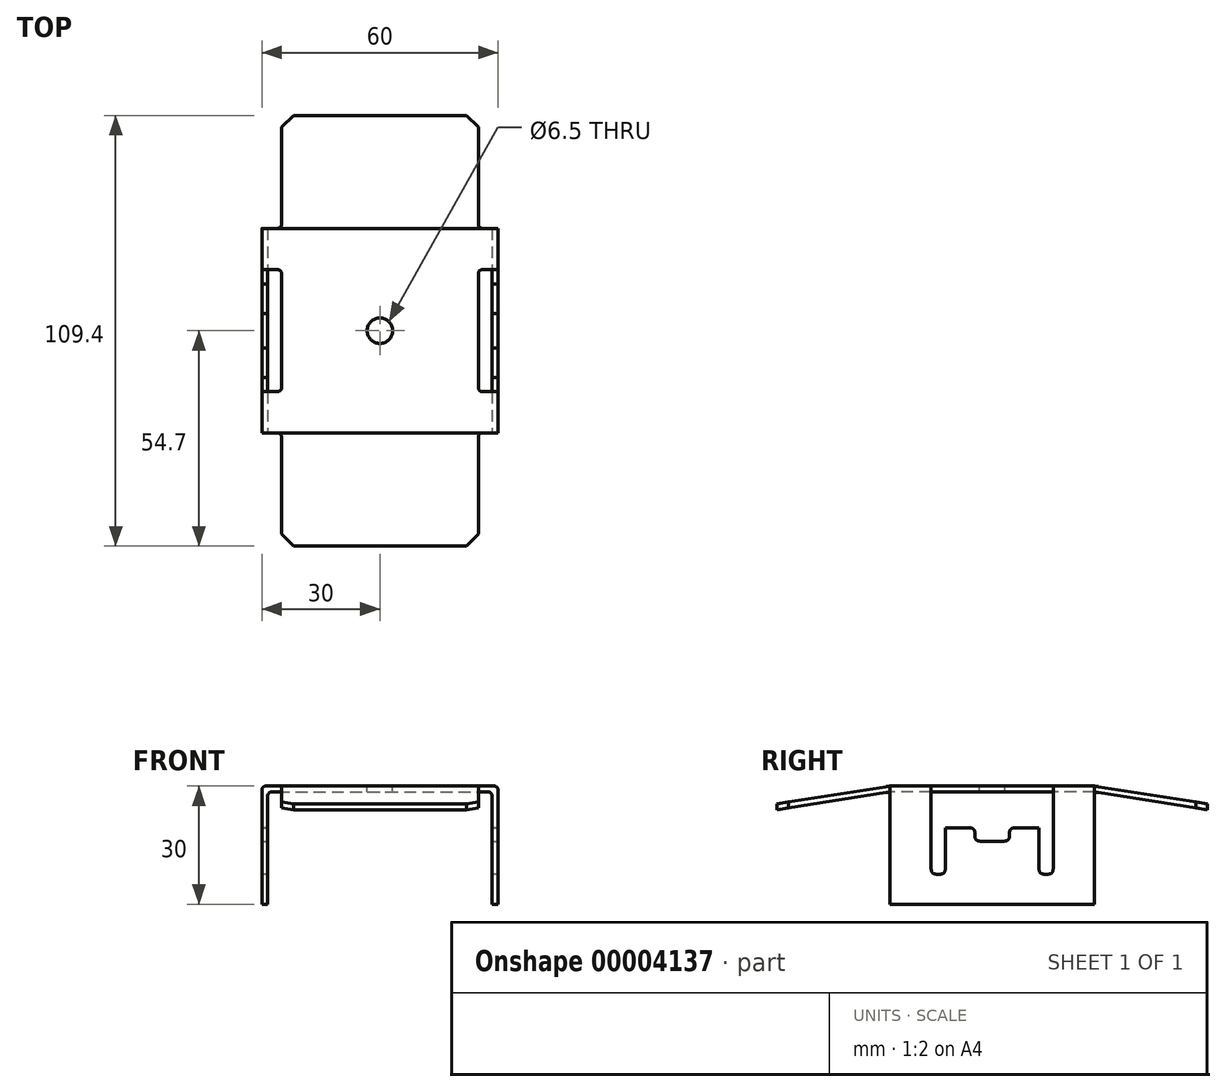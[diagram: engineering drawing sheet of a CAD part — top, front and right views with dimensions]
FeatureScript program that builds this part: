
annotation { "Feature Type Name" : "Feature", "Feature Type Description" : "" }
export const myFeature = defineFeature(function(context is Context, id is Id, definition is map)
    precondition{}
    {
        {
            var Q0;
            Q0=qCreatedBy(makeId("Top.planeOp"),FACE);
            var sketch = newSketch(context, id + "F0", { "sketchPlane" : qUnion([Q0])});
            skPoint(sketch, "E0.rect.middle", {"position": v(0, 0) * mm});
            skLineSegment(sketch, "E1", {"start": v(0, 54.7) * mm, "end": v(30, 54.7) * mm, "construction": true});
            skLineSegment(sketch, "E2", {"start": v(30, 54.7) * mm, "end": v(30, 0) * mm, "construction": true});
            skLineSegment(sketch, "E3", {"start": v(30, 0) * mm, "end": v(30, -54.7) * mm, "construction": true});
            skLineSegment(sketch, "E4", {"start": v(30, -54.7) * mm, "end": v(0, -54.7) * mm, "construction": true});
            skLineSegment(sketch, "E5", {"start": v(25, 54.7) * mm, "end": v(25, -54.7) * mm, "construction": true});
            skLineSegment(sketch, "E6", {"start": v(0, 15.5) * mm, "end": v(30, 15.5) * mm, "construction": true});
            skLineSegment(sketch, "E7", {"start": v(0, -15.5) * mm, "end": v(30, -15.5) * mm, "construction": true});
            skLineSegment(sketch, "E8", {"start": v(0, 26) * mm, "end": v(30, 26) * mm, "construction": true});
            skLineSegment(sketch, "E9", {"start": v(0, -26) * mm, "end": v(30, -26) * mm, "construction": true});
            skCircle(sketch, "E10", {"center": v(0, 0) * mm, "radius": 3.25 * mm});
            skLineSegment(sketch, "E11", {"start": v(0, 54.7) * mm, "end": v(25, 54.7) * mm});
            skLineSegment(sketch, "E12", {"start": v(25, 26) * mm, "end": v(30, 26) * mm});
            skLineSegment(sketch, "E13", {"start": v(30, -26) * mm, "end": v(25, -26) * mm});
            skLineSegment(sketch, "E14", {"start": v(25, -26) * mm, "end": v(25, -54.7) * mm});
            skLineSegment(sketch, "E15", {"start": v(0, -54.7) * mm, "end": v(25, -54.7) * mm});
            skLineSegment(sketch, "E16", {"start": v(30, -26) * mm, "end": v(30, -15.5) * mm});
            skLineSegment(sketch, "E17", {"start": v(30, 15.5) * mm, "end": v(30, 26) * mm});
            skLineSegment(sketch, "E18", {"start": v(25, 26) * mm, "end": v(25, 54.7) * mm});
            skLineSegment(sketch, "E19", {"start": v(30, 15.5) * mm, "end": v(30, -15.5) * mm});
            skLineSegment(sketch, "E20.0.MirrorCS", {"start": v(0, 54.7) * mm, "end": v(-25, 54.7) * mm});
            skLineSegment(sketch, "E20.1.MirrorCS", {"start": v(-25, 26) * mm, "end": v(-25, 54.7) * mm});
            skLineSegment(sketch, "E20.2.MirrorCS", {"start": v(-25, 26) * mm, "end": v(-30, 26) * mm});
            skLineSegment(sketch, "E20.3.MirrorCS", {"start": v(-30, 15.5) * mm, "end": v(-30, 26) * mm});
            skLineSegment(sketch, "E20.4.MirrorCS", {"start": v(-30, 15.5) * mm, "end": v(-30, -15.5) * mm});
            skLineSegment(sketch, "E20.5.MirrorCS", {"start": v(-30, -26) * mm, "end": v(-30, -15.5) * mm});
            skLineSegment(sketch, "E20.6.MirrorCS", {"start": v(-30, -26) * mm, "end": v(-25, -26) * mm});
            skLineSegment(sketch, "E20.7.MirrorCS", {"start": v(0, -54.7) * mm, "end": v(-25, -54.7) * mm});
            skLineSegment(sketch, "E20.8.MirrorCS", {"start": v(-25, -26) * mm, "end": v(-25, -54.7) * mm});
            skLineSegment(sketch, "E21", {"start": v(-30, -15.5) * mm, "end": v(-25, -15.5) * mm});
            skLineSegment(sketch, "E22", {"start": v(-25, -15.5) * mm, "end": v(-25, 15.5) * mm});
            skLineSegment(sketch, "E23", {"start": v(-25, 15.5) * mm, "end": v(-30, 15.5) * mm});
            skLineSegment(sketch, "E24", {"start": v(30, -15.5) * mm, "end": v(25, -15.5) * mm});
            skLineSegment(sketch, "E25", {"start": v(25, -15.5) * mm, "end": v(25, 15.5) * mm});
            skLineSegment(sketch, "E26", {"start": v(25, 15.5) * mm, "end": v(30, 15.5) * mm});
            skSolve(sketch);
        }
        {
            var Q0;
            Q0=qCreatedBy(makeId("Right.planeOp"),FACE);
            var sketch = newSketch(context, id + "F1", { "sketchPlane" : qUnion([Q0])});
            skLineSegment(sketch, "E27", {"start": v(0, -30) * mm, "end": v(26, -30) * mm});
            skLineSegment(sketch, "E28", {"start": v(15.5, -22.4) * mm, "end": v(11.9, -22.4) * mm});
            skLineSegment(sketch, "E29", {"start": v(11.9, -22.4) * mm, "end": v(11.9, -10.6) * mm});
            skLineSegment(sketch, "E30", {"start": v(11.9, -10.6) * mm, "end": v(4.4, -10.6) * mm});
            skLineSegment(sketch, "E31", {"start": v(4.4, -10.6) * mm, "end": v(4.4, -14) * mm});
            skLineSegment(sketch, "E32", {"start": v(4.4, -14) * mm, "end": v(0, -14) * mm});
            skLineSegment(sketch, "E33", {"start": v(26, 0) * mm, "end": v(0, 0) * mm});
            skLineSegment(sketch, "E34", {"start": v(0, -1.5) * mm, "end": v(26, -1.5) * mm});
            skLineSegment(sketch, "E35", {"start": v(26, -1.5) * mm, "end": v(26, -30) * mm});
            skLineSegment(sketch, "E36", {"start": v(15.5, -22.4) * mm, "end": v(15.5, -1.5) * mm});
            skLineSegment(sketch, "E37.0.MirrorCS", {"start": v(-15.5, -22.4) * mm, "end": v(-15.5, -1.5) * mm});
            skLineSegment(sketch, "E37.1.MirrorCS", {"start": v(-15.5, -22.4) * mm, "end": v(-11.9, -22.4) * mm});
            skLineSegment(sketch, "E37.2.MirrorCS", {"start": v(-11.9, -22.4) * mm, "end": v(-11.9, -10.6) * mm});
            skLineSegment(sketch, "E37.3.MirrorCS", {"start": v(-11.9, -10.6) * mm, "end": v(-4.4, -10.6) * mm});
            skLineSegment(sketch, "E37.4.MirrorCS", {"start": v(-4.4, -10.6) * mm, "end": v(-4.4, -14) * mm});
            skLineSegment(sketch, "E37.5.MirrorCS", {"start": v(-4.4, -14) * mm, "end": v(0, -14) * mm});
            skLineSegment(sketch, "E37.6.MirrorCS", {"start": v(-26, 0) * mm, "end": v(0, 0) * mm});
            skLineSegment(sketch, "E37.10.MirrorCS", {"start": v(0, -1.5) * mm, "end": v(-26, -1.5) * mm});
            skLineSegment(sketch, "E37.11.MirrorCS", {"start": v(0, -30) * mm, "end": v(-26, -30) * mm});
            skLineSegment(sketch, "E37.12.MirrorCS", {"start": v(-26, -1.5) * mm, "end": v(-26, -30) * mm});
            skLineSegment(sketch, "E38", {"start": v(55, 0) * mm, "end": v(55, -4.6) * mm});
            skLineSegment(sketch, "E39", {"start": v(55, 0) * mm, "end": v(26, 0) * mm});
            skLineSegment(sketch, "E40", {"start": v(55, -4.6) * mm, "end": v(55, -6.1) * mm});
            skLineSegment(sketch, "E41", {"start": v(55, -6.1) * mm, "end": v(26, -1.5) * mm});
            skLineSegment(sketch, "E42", {"start": v(55, -4.6) * mm, "end": v(26, 0) * mm});
            skLineSegment(sketch, "E43", {"start": v(26, -30) * mm, "end": v(55, -30) * mm});
            skLineSegment(sketch, "E44", {"start": v(55, -30) * mm, "end": v(55, -6.1) * mm});
            skLineSegment(sketch, "E45.0.MirrorCS", {"start": v(-55, -4.6) * mm, "end": v(-55, -6.1) * mm});
            skLineSegment(sketch, "E45.1.MirrorCS", {"start": v(-26, -30) * mm, "end": v(-55, -30) * mm});
            skLineSegment(sketch, "E45.2.MirrorCS", {"start": v(-55, -30) * mm, "end": v(-55, -6.1) * mm});
            skLineSegment(sketch, "E45.3.MirrorCS", {"start": v(-55, -6.1) * mm, "end": v(-26, -1.5) * mm});
            skLineSegment(sketch, "E45.4.MirrorCS", {"start": v(-55, -4.6) * mm, "end": v(-26, 0) * mm});
            skLineSegment(sketch, "E45.5.MirrorCS", {"start": v(-55, 0) * mm, "end": v(-26, 0) * mm});
            skLineSegment(sketch, "E45.6.MirrorCS", {"start": v(-55, 0) * mm, "end": v(-55, -4.6) * mm});
            skSolve(sketch);
        }
        {
            var Q0;
            Q0=qCreatedBy(makeId("Front.planeOp"),FACE);
            var sketch = newSketch(context, id + "F2", { "sketchPlane" : qUnion([Q0])});
            skLineSegment(sketch, "E46", {"start": v(0, 0) * mm, "end": v(-30, 0) * mm});
            skLineSegment(sketch, "E47", {"start": v(-30, 0) * mm, "end": v(-30, -30) * mm});
            skLineSegment(sketch, "E48", {"start": v(-30, -30) * mm, "end": v(-28.5, -30) * mm});
            skLineSegment(sketch, "E49", {"start": v(-28.5, -30) * mm, "end": v(-28.5, -1.5) * mm});
            skLineSegment(sketch, "E50", {"start": v(-28.5, -1.5) * mm, "end": v(0, -1.5) * mm});
            skLineSegment(sketch, "E51", {"start": v(-28.5, -30) * mm, "end": v(0, -30) * mm});
            skLineSegment(sketch, "E52", {"start": v(0, -30) * mm, "end": v(0, -1.5) * mm});
            skLineSegment(sketch, "E53.0.MirrorCS", {"start": v(28.5, -30) * mm, "end": v(0, -30) * mm});
            skLineSegment(sketch, "E53.1.MirrorCS", {"start": v(30, -30) * mm, "end": v(28.5, -30) * mm});
            skLineSegment(sketch, "E53.2.MirrorCS", {"start": v(28.5, -30) * mm, "end": v(28.5, -1.5) * mm});
            skLineSegment(sketch, "E53.3.MirrorCS", {"start": v(30, 0) * mm, "end": v(30, -30) * mm});
            skLineSegment(sketch, "E53.4.MirrorCS", {"start": v(28.5, -1.5) * mm, "end": v(0, -1.5) * mm});
            skLineSegment(sketch, "E53.5.MirrorCS", {"start": v(0, 0) * mm, "end": v(30, 0) * mm});
            skSolve(sketch);
        }
        {
            var Q0;
            Q0=makeQuery(id+"F0.imprint","IMPRINT",FACE,{"disambiguationData":[TD([[makeQuery(id+"F0.imprint","IMPRINT",EDGE,{"derivedFrom":sQuery(id+"F0.wireOp",EDGE,"E10")}),-1.0]])]});
            var Q1;
            Q1=makeQuery(id+"F0.imprint","IMPRINT",FACE,{"disambiguationData":[TD([[makeQuery(id+"F0.imprint","IMPRINT",EDGE,{"derivedFrom":sQuery(id+"F0.wireOp",EDGE,"E19")}),-1.0]])]});
            var Q2;
            Q2=makeQuery(id+"F0.imprint","IMPRINT",FACE,{"disambiguationData":[TD([[makeQuery(id+"F0.imprint","IMPRINT",EDGE,{"derivedFrom":sQuery(id+"F0.wireOp",EDGE,"E20.4.MirrorCS")}),1.0]])]});
            extrude(context, id + "F3", {"entities" : qUnion([Q0, Q1, Q2]), "oppositeDirection" : true, "depth" : 30 * mm});
        }
        {
            var Q0;
            Q0=makeQuery(id+"F1.imprint","IMPRINT",FACE,{"disambiguationData":[TD([[makeQuery(id+"F1.imprint","IMPRINT",EDGE,{"derivedFrom":sQuery(id+"F1.wireOp",EDGE,"E28")}),-1.0]])]});
            extrude(context, id + "F4", {"entities" : qUnion([Q0]), "operationType" : NewBodyOperationType.REMOVE, "endBound" : BoundingType.SYMMETRIC, "oppositeDirection" : true, "depth" : 60 * mm});
        }
        {
            var Q0;
            Q0=makeQuery(id+"F1.imprint","IMPRINT",FACE,{"disambiguationData":[TD([[makeQuery(id+"F1.imprint","IMPRINT",EDGE,{"derivedFrom":sQuery(id+"F1.wireOp",EDGE,"E45.4.MirrorCS")}),1.0]])]});
            var Q1;
            Q1=makeQuery(id+"F1.imprint","IMPRINT",FACE,{"disambiguationData":[TD([[makeQuery(id+"F1.imprint","IMPRINT",EDGE,{"derivedFrom":sQuery(id+"F1.wireOp",EDGE,"E38")}),-1.0]])]});
            var Q2;
            Q2=makeQuery(id+"F1.imprint","IMPRINT",FACE,{"disambiguationData":[TD([[makeQuery(id+"F1.imprint","IMPRINT",EDGE,{"derivedFrom":sQuery(id+"F1.wireOp",EDGE,"E35")}),1.0]])]});
            var Q3;
            Q3=makeQuery(id+"F1.imprint","IMPRINT",FACE,{"disambiguationData":[TD([[makeQuery(id+"F1.imprint","IMPRINT",EDGE,{"derivedFrom":sQuery(id+"F1.wireOp",EDGE,"E37.12.MirrorCS")}),-1.0]])]});
            extrude(context, id + "F5", {"entities" : qUnion([Q0, Q1, Q2, Q3]), "operationType" : NewBodyOperationType.REMOVE, "endBound" : BoundingType.SYMMETRIC, "oppositeDirection" : true, "depth" : 50 * mm});
        }
        {
            var Q0;
            Q0=makeQuery(id+"F2.imprint","IMPRINT",FACE,{"disambiguationData":[TD([[makeQuery(id+"F2.imprint","IMPRINT",EDGE,{"derivedFrom":sQuery(id+"F2.wireOp",EDGE,"E49")}),-1.0]])]});
            var Q1;
            Q1=makeQuery(id+"F2.imprint","IMPRINT",FACE,{"disambiguationData":[TD([[makeQuery(id+"F2.imprint","IMPRINT",EDGE,{"derivedFrom":sQuery(id+"F2.wireOp",EDGE,"E52")}),-1.0]])]});
            extrude(context, id + "F6", {"entities" : qUnion([Q0, Q1]), "operationType" : NewBodyOperationType.REMOVE, "endBound" : BoundingType.SYMMETRIC, "oppositeDirection" : true, "depth" : 52 * mm});
        }
        {
            var Q0;
            Q0=makeQuery(id+"F3.opExtrude","SWEPT_EDGE",EDGE,{"disambiguationData":[OSD([sQuery(id+"F0.wireOp",EDGE,"E20.7.MirrorCS"),sQuery(id+"F0.wireOp",EDGE,"E20.8.MirrorCS")])]});
            var Q1;
            Q1=makeQuery(id+"F3.opExtrude","SWEPT_EDGE",EDGE,{"disambiguationData":[OSD([sQuery(id+"F0.wireOp",EDGE,"E14"),sQuery(id+"F0.wireOp",EDGE,"E15")])]});
            var Q2;
            Q2=makeQuery(id+"F3.opExtrude","SWEPT_EDGE",EDGE,{"disambiguationData":[OSD([sQuery(id+"F0.wireOp",EDGE,"E11"),sQuery(id+"F0.wireOp",EDGE,"E18")])]});
            var Q3;
            Q3=makeQuery(id+"F3.opExtrude","SWEPT_EDGE",EDGE,{"disambiguationData":[OSD([sQuery(id+"F0.wireOp",EDGE,"E20.0.MirrorCS"),sQuery(id+"F0.wireOp",EDGE,"E20.1.MirrorCS")])]});
            var Q4;
            {var subQ0=sQuery(id+"F0.wireOp",EDGE,"E13");var subQ1=sQuery(id+"F0.wireOp",EDGE,"E20.6.MirrorCS");var subQ2=sQuery(id+"F1.wireOp",EDGE,"E37.12.MirrorCS");Q4=makeQuery(id+"F6.boolean.opBoolean","SPLIT",EDGE,{"disambiguationData":[TD([makeQuery(id+"F6.opExtrude","SWEPT_FACE",FACE,{"disambiguationData":[OSD([sQuery(id+"F2.wireOp",EDGE,"E53.2.MirrorCS")])]})])],"derivedFrom":makeQuery(id+"F5.boolean.opBoolean","MERGE",EDGE,{"derivedFrom":[makeQuery(id+"F3.opExtrude","CAP_EDGE",EDGE,{"disambiguationData":[OSD([subQ0])],"isStart":false}),makeQuery(id+"F3.opExtrude","CAP_EDGE",EDGE,{"disambiguationData":[OSD([subQ1])],"isStart":false}),makeQuery(id+"F5.opExtrude","SWEPT_EDGE",EDGE,{"disambiguationData":[OSD([sQuery(id+"F1.wireOp",EDGE,"E37.11.MirrorCS"),subQ2,sQuery(id+"F1.wireOp",EDGE,"E45.1.MirrorCS")])]})]})});}
            var Q5;
            {var subQ0=sQuery(id+"F0.wireOp",EDGE,"E13");var subQ1=sQuery(id+"F0.wireOp",EDGE,"E20.6.MirrorCS");var subQ2=sQuery(id+"F1.wireOp",EDGE,"E37.12.MirrorCS");Q5=makeQuery(id+"F6.boolean.opBoolean","SPLIT",EDGE,{"disambiguationData":[TD([makeQuery(id+"F6.opExtrude","SWEPT_FACE",FACE,{"disambiguationData":[OSD([sQuery(id+"F2.wireOp",EDGE,"E49")])]})])],"derivedFrom":makeQuery(id+"F5.boolean.opBoolean","MERGE",EDGE,{"derivedFrom":[makeQuery(id+"F3.opExtrude","CAP_EDGE",EDGE,{"disambiguationData":[OSD([subQ0])],"isStart":false}),makeQuery(id+"F3.opExtrude","CAP_EDGE",EDGE,{"disambiguationData":[OSD([subQ1])],"isStart":false}),makeQuery(id+"F5.opExtrude","SWEPT_EDGE",EDGE,{"disambiguationData":[OSD([sQuery(id+"F1.wireOp",EDGE,"E37.11.MirrorCS"),subQ2,sQuery(id+"F1.wireOp",EDGE,"E45.1.MirrorCS")])]})]})});}
            var Q6;
            {var subQ0=sQuery(id+"F0.wireOp",EDGE,"E12");var subQ1=sQuery(id+"F0.wireOp",EDGE,"E20.2.MirrorCS");var subQ2=sQuery(id+"F1.wireOp",EDGE,"E35");Q6=makeQuery(id+"F6.boolean.opBoolean","SPLIT",EDGE,{"disambiguationData":[TD([makeQuery(id+"F6.opExtrude","SWEPT_FACE",FACE,{"disambiguationData":[OSD([sQuery(id+"F2.wireOp",EDGE,"E53.2.MirrorCS")])]})])],"derivedFrom":makeQuery(id+"F5.boolean.opBoolean","MERGE",EDGE,{"derivedFrom":[makeQuery(id+"F3.opExtrude","CAP_EDGE",EDGE,{"disambiguationData":[OSD([subQ0])],"isStart":false}),makeQuery(id+"F3.opExtrude","CAP_EDGE",EDGE,{"disambiguationData":[OSD([subQ1])],"isStart":false}),makeQuery(id+"F5.opExtrude","SWEPT_EDGE",EDGE,{"disambiguationData":[OSD([sQuery(id+"F1.wireOp",EDGE,"E27"),subQ2,sQuery(id+"F1.wireOp",EDGE,"E43")])]})]})});}
            var Q7;
            {var subQ0=sQuery(id+"F0.wireOp",EDGE,"E12");var subQ1=sQuery(id+"F0.wireOp",EDGE,"E20.2.MirrorCS");var subQ2=sQuery(id+"F1.wireOp",EDGE,"E35");Q7=makeQuery(id+"F6.boolean.opBoolean","SPLIT",EDGE,{"disambiguationData":[TD([makeQuery(id+"F6.opExtrude","SWEPT_FACE",FACE,{"disambiguationData":[OSD([sQuery(id+"F2.wireOp",EDGE,"E49")])]})])],"derivedFrom":makeQuery(id+"F5.boolean.opBoolean","MERGE",EDGE,{"derivedFrom":[makeQuery(id+"F3.opExtrude","CAP_EDGE",EDGE,{"disambiguationData":[OSD([subQ0])],"isStart":false}),makeQuery(id+"F3.opExtrude","CAP_EDGE",EDGE,{"disambiguationData":[OSD([subQ1])],"isStart":false}),makeQuery(id+"F5.opExtrude","SWEPT_EDGE",EDGE,{"disambiguationData":[OSD([sQuery(id+"F1.wireOp",EDGE,"E27"),subQ2,sQuery(id+"F1.wireOp",EDGE,"E43")])]})]})});}
            chamfer(context, id + "F7", {"entities" : qUnion([Q0, Q1, Q2, Q3, Q4, Q5, Q6, Q7]), "width" : 3 * mm, "tangentPropagation" : true});
        }
        {
            var Q0;
            Q0=makeQuery(id+"F0.imprint","IMPRINT",FACE,{"disambiguationData":[TD([[makeQuery(id+"F0.imprint","IMPRINT",EDGE,{"derivedFrom":sQuery(id+"F0.wireOp",EDGE,"E19")}),-1.0]])]});
            var Q1;
            Q1=makeQuery(id+"F0.imprint","IMPRINT",FACE,{"disambiguationData":[TD([[makeQuery(id+"F0.imprint","IMPRINT",EDGE,{"derivedFrom":sQuery(id+"F0.wireOp",EDGE,"E20.4.MirrorCS")}),1.0]])]});
            extrude(context, id + "F8", {"entities" : qUnion([Q0, Q1]), "operationType" : NewBodyOperationType.REMOVE, "oppositeDirection" : true, "depth" : 2 * mm});
        }
        {
            var Q0;
            {var subQ0=sQuery(id+"F1.wireOp",EDGE,"E30");var subQ1=sQuery(id+"F1.wireOp",EDGE,"E31");Q0=makeQuery(id+"F6.boolean.opBoolean","SPLIT",EDGE,{"disambiguationData":[TD([makeQuery(id+"F6.opExtrude","SWEPT_FACE",FACE,{"disambiguationData":[OSD([sQuery(id+"F2.wireOp",EDGE,"E53.2.MirrorCS")])]})])],"derivedFrom":makeQuery(id+"F4.boolean.opBoolean","COPY",EDGE,{"derivedFrom":makeQuery(id+"F4.opExtrude","SWEPT_EDGE",EDGE,{"disambiguationData":[OSD([subQ0,subQ1])]})})});}
            var Q1;
            {var subQ0=sQuery(id+"F1.wireOp",EDGE,"E37.3.MirrorCS");var subQ1=sQuery(id+"F1.wireOp",EDGE,"E37.4.MirrorCS");Q1=makeQuery(id+"F6.boolean.opBoolean","SPLIT",EDGE,{"disambiguationData":[TD([makeQuery(id+"F6.opExtrude","SWEPT_FACE",FACE,{"disambiguationData":[OSD([sQuery(id+"F2.wireOp",EDGE,"E53.2.MirrorCS")])]})])],"derivedFrom":makeQuery(id+"F4.boolean.opBoolean","COPY",EDGE,{"derivedFrom":makeQuery(id+"F4.opExtrude","SWEPT_EDGE",EDGE,{"disambiguationData":[OSD([subQ0,subQ1])]})})});}
            var Q2;
            {var subQ0=sQuery(id+"F1.wireOp",EDGE,"E31");var subQ1=sQuery(id+"F1.wireOp",EDGE,"E32");Q2=makeQuery(id+"F6.boolean.opBoolean","SPLIT",EDGE,{"disambiguationData":[TD([makeQuery(id+"F6.opExtrude","SWEPT_FACE",FACE,{"disambiguationData":[OSD([sQuery(id+"F2.wireOp",EDGE,"E53.2.MirrorCS")])]})])],"derivedFrom":makeQuery(id+"F4.boolean.opBoolean","COPY",EDGE,{"derivedFrom":makeQuery(id+"F4.opExtrude","SWEPT_EDGE",EDGE,{"disambiguationData":[OSD([subQ0,subQ1])]})})});}
            var Q3;
            {var subQ0=sQuery(id+"F1.wireOp",EDGE,"E37.4.MirrorCS");var subQ1=sQuery(id+"F1.wireOp",EDGE,"E37.5.MirrorCS");Q3=makeQuery(id+"F6.boolean.opBoolean","SPLIT",EDGE,{"disambiguationData":[TD([makeQuery(id+"F6.opExtrude","SWEPT_FACE",FACE,{"disambiguationData":[OSD([sQuery(id+"F2.wireOp",EDGE,"E53.2.MirrorCS")])]})])],"derivedFrom":makeQuery(id+"F4.boolean.opBoolean","COPY",EDGE,{"derivedFrom":makeQuery(id+"F4.opExtrude","SWEPT_EDGE",EDGE,{"disambiguationData":[OSD([subQ0,subQ1])]})})});}
            var Q4;
            {var subQ0=sQuery(id+"F1.wireOp",EDGE,"E37.0.MirrorCS");var subQ1=sQuery(id+"F1.wireOp",EDGE,"E37.1.MirrorCS");Q4=makeQuery(id+"F6.boolean.opBoolean","SPLIT",EDGE,{"disambiguationData":[TD([makeQuery(id+"F6.opExtrude","SWEPT_FACE",FACE,{"disambiguationData":[OSD([sQuery(id+"F2.wireOp",EDGE,"E53.2.MirrorCS")])]})])],"derivedFrom":makeQuery(id+"F4.boolean.opBoolean","COPY",EDGE,{"derivedFrom":makeQuery(id+"F4.opExtrude","SWEPT_EDGE",EDGE,{"disambiguationData":[OSD([subQ0,subQ1])]})})});}
            var Q5;
            {var subQ0=sQuery(id+"F1.wireOp",EDGE,"E37.1.MirrorCS");var subQ1=sQuery(id+"F1.wireOp",EDGE,"E37.2.MirrorCS");Q5=makeQuery(id+"F6.boolean.opBoolean","SPLIT",EDGE,{"disambiguationData":[TD([makeQuery(id+"F6.opExtrude","SWEPT_FACE",FACE,{"disambiguationData":[OSD([sQuery(id+"F2.wireOp",EDGE,"E53.2.MirrorCS")])]})])],"derivedFrom":makeQuery(id+"F4.boolean.opBoolean","COPY",EDGE,{"derivedFrom":makeQuery(id+"F4.opExtrude","SWEPT_EDGE",EDGE,{"disambiguationData":[OSD([subQ0,subQ1])]})})});}
            var Q6;
            {var subQ0=sQuery(id+"F1.wireOp",EDGE,"E28");var subQ1=sQuery(id+"F1.wireOp",EDGE,"E36");Q6=makeQuery(id+"F6.boolean.opBoolean","SPLIT",EDGE,{"disambiguationData":[TD([makeQuery(id+"F6.opExtrude","SWEPT_FACE",FACE,{"disambiguationData":[OSD([sQuery(id+"F2.wireOp",EDGE,"E53.2.MirrorCS")])]})])],"derivedFrom":makeQuery(id+"F4.boolean.opBoolean","COPY",EDGE,{"derivedFrom":makeQuery(id+"F4.opExtrude","SWEPT_EDGE",EDGE,{"disambiguationData":[OSD([subQ0,subQ1])]})})});}
            var Q7;
            {var subQ0=sQuery(id+"F1.wireOp",EDGE,"E28");var subQ1=sQuery(id+"F1.wireOp",EDGE,"E29");Q7=makeQuery(id+"F6.boolean.opBoolean","SPLIT",EDGE,{"disambiguationData":[TD([makeQuery(id+"F6.opExtrude","SWEPT_FACE",FACE,{"disambiguationData":[OSD([sQuery(id+"F2.wireOp",EDGE,"E53.2.MirrorCS")])]})])],"derivedFrom":makeQuery(id+"F4.boolean.opBoolean","COPY",EDGE,{"derivedFrom":makeQuery(id+"F4.opExtrude","SWEPT_EDGE",EDGE,{"disambiguationData":[OSD([subQ0,subQ1])]})})});}
            var Q8;
            {var subQ0=sQuery(id+"F1.wireOp",EDGE,"E28");var subQ1=sQuery(id+"F1.wireOp",EDGE,"E36");Q8=makeQuery(id+"F6.boolean.opBoolean","SPLIT",EDGE,{"disambiguationData":[TD([makeQuery(id+"F6.opExtrude","SWEPT_FACE",FACE,{"disambiguationData":[OSD([sQuery(id+"F2.wireOp",EDGE,"E49")])]})])],"derivedFrom":makeQuery(id+"F4.boolean.opBoolean","COPY",EDGE,{"derivedFrom":makeQuery(id+"F4.opExtrude","SWEPT_EDGE",EDGE,{"disambiguationData":[OSD([subQ0,subQ1])]})})});}
            var Q9;
            {var subQ0=sQuery(id+"F1.wireOp",EDGE,"E37.1.MirrorCS");var subQ1=sQuery(id+"F1.wireOp",EDGE,"E37.2.MirrorCS");Q9=makeQuery(id+"F6.boolean.opBoolean","SPLIT",EDGE,{"disambiguationData":[TD([makeQuery(id+"F6.opExtrude","SWEPT_FACE",FACE,{"disambiguationData":[OSD([sQuery(id+"F2.wireOp",EDGE,"E49")])]})])],"derivedFrom":makeQuery(id+"F4.boolean.opBoolean","COPY",EDGE,{"derivedFrom":makeQuery(id+"F4.opExtrude","SWEPT_EDGE",EDGE,{"disambiguationData":[OSD([subQ0,subQ1])]})})});}
            var Q10;
            {var subQ0=sQuery(id+"F1.wireOp",EDGE,"E31");var subQ1=sQuery(id+"F1.wireOp",EDGE,"E32");Q10=makeQuery(id+"F6.boolean.opBoolean","SPLIT",EDGE,{"disambiguationData":[TD([makeQuery(id+"F6.opExtrude","SWEPT_FACE",FACE,{"disambiguationData":[OSD([sQuery(id+"F2.wireOp",EDGE,"E49")])]})])],"derivedFrom":makeQuery(id+"F4.boolean.opBoolean","COPY",EDGE,{"derivedFrom":makeQuery(id+"F4.opExtrude","SWEPT_EDGE",EDGE,{"disambiguationData":[OSD([subQ0,subQ1])]})})});}
            var Q11;
            {var subQ0=sQuery(id+"F1.wireOp",EDGE,"E28");var subQ1=sQuery(id+"F1.wireOp",EDGE,"E29");Q11=makeQuery(id+"F6.boolean.opBoolean","SPLIT",EDGE,{"disambiguationData":[TD([makeQuery(id+"F6.opExtrude","SWEPT_FACE",FACE,{"disambiguationData":[OSD([sQuery(id+"F2.wireOp",EDGE,"E49")])]})])],"derivedFrom":makeQuery(id+"F4.boolean.opBoolean","COPY",EDGE,{"derivedFrom":makeQuery(id+"F4.opExtrude","SWEPT_EDGE",EDGE,{"disambiguationData":[OSD([subQ0,subQ1])]})})});}
            var Q12;
            {var subQ0=sQuery(id+"F1.wireOp",EDGE,"E37.4.MirrorCS");var subQ1=sQuery(id+"F1.wireOp",EDGE,"E37.5.MirrorCS");Q12=makeQuery(id+"F6.boolean.opBoolean","SPLIT",EDGE,{"disambiguationData":[TD([makeQuery(id+"F6.opExtrude","SWEPT_FACE",FACE,{"disambiguationData":[OSD([sQuery(id+"F2.wireOp",EDGE,"E49")])]})])],"derivedFrom":makeQuery(id+"F4.boolean.opBoolean","COPY",EDGE,{"derivedFrom":makeQuery(id+"F4.opExtrude","SWEPT_EDGE",EDGE,{"disambiguationData":[OSD([subQ0,subQ1])]})})});}
            var Q13;
            {var subQ0=sQuery(id+"F1.wireOp",EDGE,"E37.0.MirrorCS");var subQ1=sQuery(id+"F1.wireOp",EDGE,"E37.1.MirrorCS");Q13=makeQuery(id+"F6.boolean.opBoolean","SPLIT",EDGE,{"disambiguationData":[TD([makeQuery(id+"F6.opExtrude","SWEPT_FACE",FACE,{"disambiguationData":[OSD([sQuery(id+"F2.wireOp",EDGE,"E49")])]})])],"derivedFrom":makeQuery(id+"F4.boolean.opBoolean","COPY",EDGE,{"derivedFrom":makeQuery(id+"F4.opExtrude","SWEPT_EDGE",EDGE,{"disambiguationData":[OSD([subQ0,subQ1])]})})});}
            var Q14;
            {var subQ0=sQuery(id+"F1.wireOp",EDGE,"E37.3.MirrorCS");var subQ1=sQuery(id+"F1.wireOp",EDGE,"E37.4.MirrorCS");Q14=makeQuery(id+"F6.boolean.opBoolean","SPLIT",EDGE,{"disambiguationData":[TD([makeQuery(id+"F6.opExtrude","SWEPT_FACE",FACE,{"disambiguationData":[OSD([sQuery(id+"F2.wireOp",EDGE,"E49")])]})])],"derivedFrom":makeQuery(id+"F4.boolean.opBoolean","COPY",EDGE,{"derivedFrom":makeQuery(id+"F4.opExtrude","SWEPT_EDGE",EDGE,{"disambiguationData":[OSD([subQ0,subQ1])]})})});}
            var Q15;
            {var subQ0=sQuery(id+"F1.wireOp",EDGE,"E30");var subQ1=sQuery(id+"F1.wireOp",EDGE,"E31");Q15=makeQuery(id+"F6.boolean.opBoolean","SPLIT",EDGE,{"disambiguationData":[TD([makeQuery(id+"F6.opExtrude","SWEPT_FACE",FACE,{"disambiguationData":[OSD([sQuery(id+"F2.wireOp",EDGE,"E49")])]})])],"derivedFrom":makeQuery(id+"F4.boolean.opBoolean","COPY",EDGE,{"derivedFrom":makeQuery(id+"F4.opExtrude","SWEPT_EDGE",EDGE,{"disambiguationData":[OSD([subQ0,subQ1])]})})});}
            fillet(context, id + "F9", {"entities" : qUnion([Q0, Q1, Q2, Q3, Q4, Q5, Q6, Q7, Q8, Q9, Q10, Q11, Q12, Q13, Q14, Q15]), "radius" : 1.4 * mm, "tangentPropagation" : true, "rho" : 0.5, "crossSection" : FilletCrossSection.CONIC, "allowEdgeOverflow" : false});
        }
        {
            var Q0;
            Q0=makeQuery(id+"F8.boolean.opBoolean","COPY",EDGE,{"derivedFrom":makeQuery(id+"F8.opExtrude","SWEPT_EDGE",EDGE,{"disambiguationData":[OSD([sQuery(id+"F0.wireOp",EDGE,"E25"),sQuery(id+"F0.wireOp",EDGE,"E26")])]})});
            var Q1;
            Q1=makeQuery(id+"F8.boolean.opBoolean","COPY",EDGE,{"derivedFrom":makeQuery(id+"F8.opExtrude","SWEPT_EDGE",EDGE,{"disambiguationData":[OSD([sQuery(id+"F0.wireOp",EDGE,"E24"),sQuery(id+"F0.wireOp",EDGE,"E25")])]})});
            var Q2;
            Q2=makeQuery(id+"F3.opExtrude","SWEPT_EDGE",EDGE,{"disambiguationData":[OSD([sQuery(id+"F0.wireOp",EDGE,"E13"),sQuery(id+"F0.wireOp",EDGE,"E14")])]});
            var Q3;
            {var subQ0=sQuery(id+"F0.wireOp",EDGE,"E16");var subQ1=sQuery(id+"F0.wireOp",EDGE,"E17");var subQ2=sQuery(id+"F0.wireOp",EDGE,"E19");var subQ4=sQuery(id+"F0.wireOp",EDGE,"E13");Q3=makeQuery(id+"F8.boolean.opBoolean","SPLIT",EDGE,{"disambiguationData":[TD([makeQuery(id+"F3.opExtrude","SWEPT_FACE",FACE,{"disambiguationData":[OSD([subQ4])]})])],"derivedFrom":makeQuery(id+"F3.opExtrude","CAP_EDGE",EDGE,{"disambiguationData":[OSD([subQ0,subQ1,subQ2])],"isStart":true})});}
            var Q4;
            {var subQ0=sQuery(id+"F0.wireOp",EDGE,"E16");var subQ1=sQuery(id+"F0.wireOp",EDGE,"E17");var subQ2=sQuery(id+"F0.wireOp",EDGE,"E19");var subQ4=sQuery(id+"F0.wireOp",EDGE,"E12");Q4=makeQuery(id+"F8.boolean.opBoolean","SPLIT",EDGE,{"disambiguationData":[TD([makeQuery(id+"F3.opExtrude","SWEPT_FACE",FACE,{"disambiguationData":[OSD([subQ4])]})])],"derivedFrom":makeQuery(id+"F3.opExtrude","CAP_EDGE",EDGE,{"disambiguationData":[OSD([subQ0,subQ1,subQ2])],"isStart":true})});}
            var Q5;
            Q5=makeQuery(id+"F3.opExtrude","SWEPT_EDGE",EDGE,{"disambiguationData":[OSD([sQuery(id+"F0.wireOp",EDGE,"E12"),sQuery(id+"F0.wireOp",EDGE,"E18")])]});
            var Q6;
            Q6=makeQuery(id+"F3.opExtrude","SWEPT_EDGE",EDGE,{"disambiguationData":[OSD([sQuery(id+"F0.wireOp",EDGE,"E20.1.MirrorCS"),sQuery(id+"F0.wireOp",EDGE,"E20.2.MirrorCS")])]});
            var Q7;
            {var subQ0=sQuery(id+"F0.wireOp",EDGE,"E20.3.MirrorCS");var subQ1=sQuery(id+"F0.wireOp",EDGE,"E20.4.MirrorCS");var subQ2=sQuery(id+"F0.wireOp",EDGE,"E20.5.MirrorCS");var subQ4=sQuery(id+"F0.wireOp",EDGE,"E12");Q7=makeQuery(id+"F8.boolean.opBoolean","SPLIT",EDGE,{"disambiguationData":[TD([makeQuery(id+"F3.opExtrude","SWEPT_FACE",FACE,{"disambiguationData":[OSD([subQ4])]})])],"derivedFrom":makeQuery(id+"F3.opExtrude","CAP_EDGE",EDGE,{"disambiguationData":[OSD([subQ0,subQ1,subQ2])],"isStart":true})});}
            var Q8;
            Q8=makeQuery(id+"F8.boolean.opBoolean","COPY",EDGE,{"derivedFrom":makeQuery(id+"F8.opExtrude","SWEPT_EDGE",EDGE,{"disambiguationData":[OSD([sQuery(id+"F0.wireOp",EDGE,"E22"),sQuery(id+"F0.wireOp",EDGE,"E23")])]})});
            var Q9;
            {var subQ0=sQuery(id+"F0.wireOp",EDGE,"E20.3.MirrorCS");var subQ1=sQuery(id+"F0.wireOp",EDGE,"E20.4.MirrorCS");var subQ2=sQuery(id+"F0.wireOp",EDGE,"E20.5.MirrorCS");var subQ4=sQuery(id+"F0.wireOp",EDGE,"E13");Q9=makeQuery(id+"F8.boolean.opBoolean","SPLIT",EDGE,{"disambiguationData":[TD([makeQuery(id+"F3.opExtrude","SWEPT_FACE",FACE,{"disambiguationData":[OSD([subQ4])]})])],"derivedFrom":makeQuery(id+"F3.opExtrude","CAP_EDGE",EDGE,{"disambiguationData":[OSD([subQ0,subQ1,subQ2])],"isStart":true})});}
            var Q10;
            Q10=makeQuery(id+"F3.opExtrude","SWEPT_EDGE",EDGE,{"disambiguationData":[OSD([sQuery(id+"F0.wireOp",EDGE,"E20.6.MirrorCS"),sQuery(id+"F0.wireOp",EDGE,"E20.8.MirrorCS")])]});
            var Q11;
            Q11=makeQuery(id+"F8.boolean.opBoolean","COPY",EDGE,{"derivedFrom":makeQuery(id+"F8.opExtrude","SWEPT_EDGE",EDGE,{"disambiguationData":[OSD([sQuery(id+"F0.wireOp",EDGE,"E21"),sQuery(id+"F0.wireOp",EDGE,"E22")])]})});
            var Q12;
            Q12=makeQuery(id+"F3.opExtrude","SWEPT_EDGE",EDGE,{"disambiguationData":[OSD([sQuery(id+"F0.wireOp",EDGE,"E20.6.MirrorCS"),sQuery(id+"F0.wireOp",EDGE,"E20.8.MirrorCS")])]});
            var Q13;
            Q13=makeQuery(id+"F6.boolean.opBoolean","COPY",EDGE,{"disambiguationData":[OD(0.0)],"derivedFrom":makeQuery(id+"F6.opExtrude","SWEPT_EDGE",EDGE,{"disambiguationData":[OSD([sQuery(id+"F2.wireOp",EDGE,"E49"),sQuery(id+"F2.wireOp",EDGE,"E50")])]})});
            var Q14;
            Q14=makeQuery(id+"F6.boolean.opBoolean","COPY",EDGE,{"disambiguationData":[OD(1.0)],"derivedFrom":makeQuery(id+"F6.opExtrude","SWEPT_EDGE",EDGE,{"disambiguationData":[OSD([sQuery(id+"F2.wireOp",EDGE,"E49"),sQuery(id+"F2.wireOp",EDGE,"E50")])]})});
            var Q15;
            Q15=makeQuery(id+"F6.boolean.opBoolean","COPY",EDGE,{"disambiguationData":[OD(0.0)],"derivedFrom":makeQuery(id+"F6.opExtrude","SWEPT_EDGE",EDGE,{"disambiguationData":[OSD([sQuery(id+"F2.wireOp",EDGE,"E53.2.MirrorCS"),sQuery(id+"F2.wireOp",EDGE,"E53.4.MirrorCS")])]})});
            var Q16;
            Q16=makeQuery(id+"F6.boolean.opBoolean","COPY",EDGE,{"disambiguationData":[OD(1.0)],"derivedFrom":makeQuery(id+"F6.opExtrude","SWEPT_EDGE",EDGE,{"disambiguationData":[OSD([sQuery(id+"F2.wireOp",EDGE,"E53.2.MirrorCS"),sQuery(id+"F2.wireOp",EDGE,"E53.4.MirrorCS")])]})});
            fillet(context, id + "F10", {"entities" : qUnion([Q0, Q1, Q2, Q3, Q4, Q5, Q6, Q7, Q8, Q9, Q10, Q11, Q12, Q13, Q14, Q15, Q16]), "radius" : 1 * mm, "tangentPropagation" : true, "allowEdgeOverflow" : false});
        }
    });
